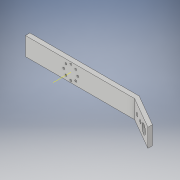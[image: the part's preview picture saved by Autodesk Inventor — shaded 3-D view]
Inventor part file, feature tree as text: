
AUTODESK INVENTOR PART (.ipt)
format: ipt  version: 2019 (Build 230136000, 136)  size: 154,112 bytes
history: native  units: in
note: dims shown in document units (in); Inventor stores cm internally (conversion verified against a paired STEP export)
features: sketch x4, extrude x3, hole x1, other x1
ambient origin geometry x8: Origin, YZ Plane, XZ Plane, XY Plane, X Axis, Y Axis, Z Axis, Center Point
bodies: Solid1 (feature_tree)
feature tree (9):
  extrude  "Extrusion1"  Depth=1.0in
  sketch  "Sketch4"  dims[d2=0.25in d3=0.0in d53=2.0in]
  extrude  "Extrusion9"  Depth=0.25in
  extrude  "Extrusion10"  Depth=2.0in
  hole  "Hole1"  [1 undecoded]
  other  "Work Axis1"
  sketch  "Sketch1"  dims[d0=6.0in d1=1.0in]
  sketch  "Sketch9"  dims[d54=30.0deg d55=2.0in]
  sketch  "Sketch10"  dims[d56=30.0deg d57=1.0in d58=0.0in d59=1.0in d60=0.5in d61=0.5in d62=0.5in d63=0.5in d64=1.0in d65=1.5in d66=0.184in d67=0.184in d68=0.5in d69=1.0in d70=0.0in d71=0.107in d72=0.385in d73=0.0in d74=3.1496in d76=360.0deg d78=0.107in d79=0.236in d80=0.375in d81=0.25in d82=0.5635in d83=1.0in d84=0.8108in d85=1.0in d86=0.5in d87=3.5in]
note: 1 required parameter value undecoded (feature->parameter linkage not recoverable at this tier; creation-order binding heuristic only, values carry confidence <= 0.55)
